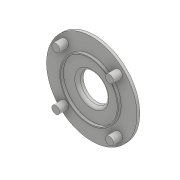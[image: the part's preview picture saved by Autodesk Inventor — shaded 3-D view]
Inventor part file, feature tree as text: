
AUTODESK INVENTOR PART (.ipt)
format: ipt  version: 2017 (Build 210142000, 142)  size: 143,872 bytes
history: native  units: mm
features: extrude x5, sketch x5, pattern_circular x1, fillet x1, projected_geometry x1
ambient origin geometry x8: Origin, YZ Plane, XZ Plane, XY Plane, X Axis, Y Axis, Z Axis, Center Point
bodies: Solid1 (feature_tree)
feature tree (13):
  extrude  "Extrusion1"  Depth=2.0mm TaperAngle=0.0deg
  extrude  "Extrusion2"  Depth=40.0mm
  extrude  "Extrusion4"  Depth=2.0mm
  pattern_circular  "Circular Pattern1"  [2 undecoded]
  extrude  "Extrusion5"  Depth=2.0mm TaperAngle=360.0deg
  extrude  "Extrusion6"  Depth=24.5mm
  fillet  "Fillet1"  Radius=24.5mm
  sketch  "Sketch1"  dims[d0=64.0mm d1=2.0mm d2=0.0mm]
  sketch  "Sketch2"  dims[d3=41.5mm d4=40.0mm]
  sketch  "Sketch4"  dims[d5=2.0mm d6=0.0mm d9=5.5mm]
  sketch  "Sketch5"  dims[d10=19.0mm]
  sketch  "Sketch6"  dims[d11=19.0mm d12=6.5mm d13=0.0mm d14=40.0mm d15=360.0deg d17=24.5mm d18=24.5mm d19=2.0mm d20=0.0mm d21=20.0mm d22=2.0mm d23=0.0mm d24=2.0mm]
  projected_geometry  "Projected Loop2"
note: 2 required parameter values undecoded (feature->parameter linkage not recoverable at this tier; creation-order binding heuristic only, values carry confidence <= 0.55)
